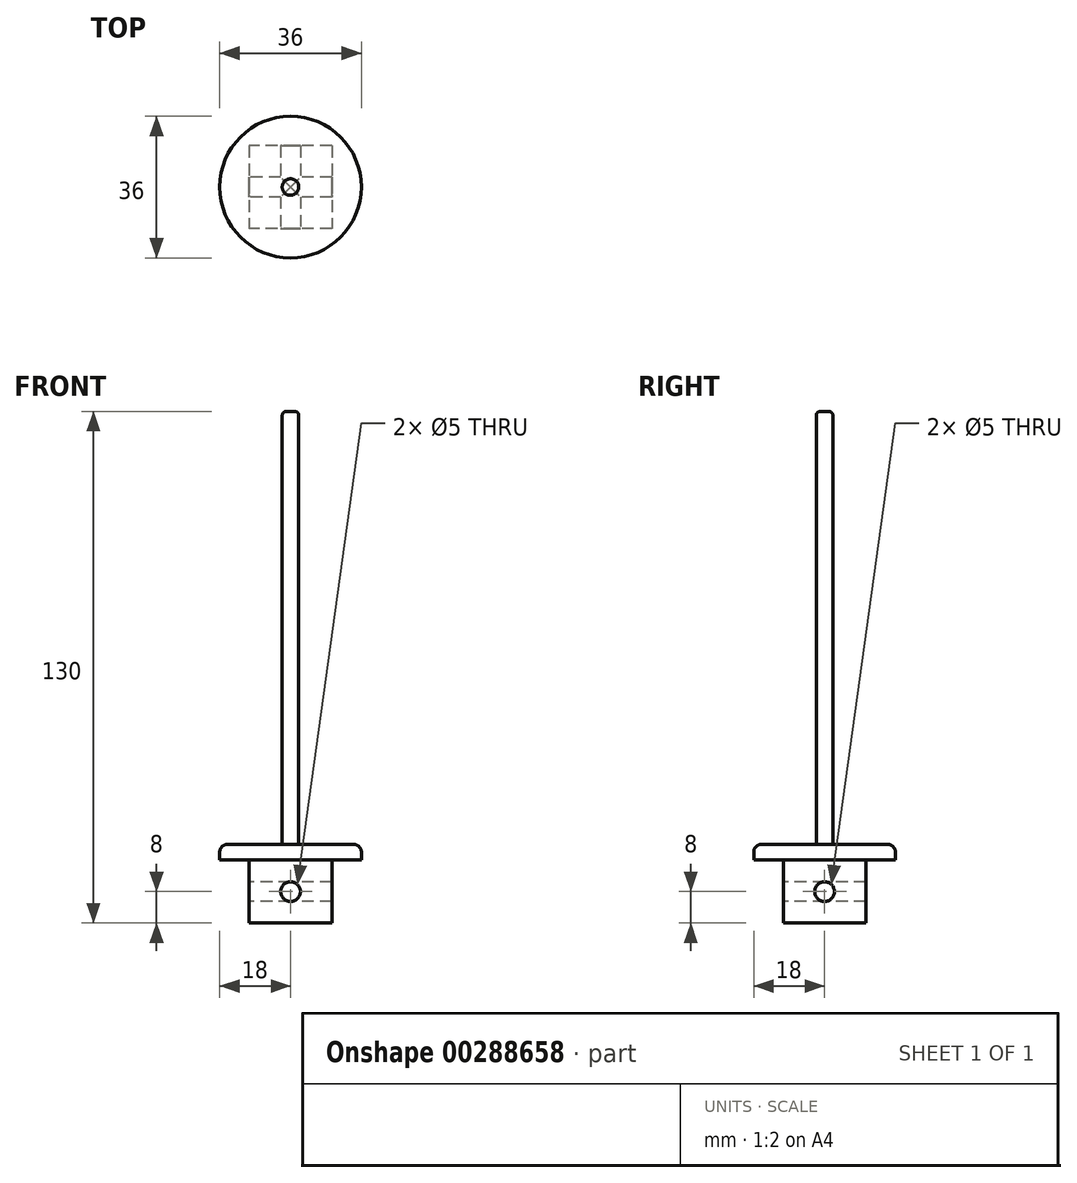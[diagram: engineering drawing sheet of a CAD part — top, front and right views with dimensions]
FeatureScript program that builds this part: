
annotation { "Feature Type Name" : "Feature", "Feature Type Description" : "" }
export const myFeature = defineFeature(function(context is Context, id is Id, definition is map)
    precondition{}
    {
        {
            var Q0;
            Q0=qCreatedBy(makeId("Top.planeOp"),FACE);
            var sketch = newSketch(context, id + "F0", { "sketchPlane" : qUnion([Q0])});
            skCircle(sketch, "E0", {"center": v(0, 0) * mm, "radius": 18 * mm});
            skSolve(sketch);
        }
        {
            var Q0;
            Q0 = qSketchRegion(id + "F0", true);
            extrude(context, id + "F1", {"entities" : qUnion([Q0]), "depth" : 4 * mm});
        }
        {
            var Q0;
            Q0=qCreatedBy(makeId("Top.planeOp"),FACE);
            var sketch = newSketch(context, id + "F2", { "sketchPlane" : qUnion([Q0])});
            skLineSegment(sketch, "E1.bottom", {"start": v(10.5, 10.5) * mm, "end": v(-10.5, 10.5) * mm});
            skLineSegment(sketch, "E1.top", {"start": v(10.5, -10.5) * mm, "end": v(-10.5, -10.5) * mm});
            skLineSegment(sketch, "E1.left", {"start": v(10.5, 10.5) * mm, "end": v(10.5, -10.5) * mm});
            skLineSegment(sketch, "E1.right", {"start": v(-10.5, 10.5) * mm, "end": v(-10.5, -10.5) * mm});
            skPoint(sketch, "E1.middle", {"position": v(0, 0) * mm});
            skSolve(sketch);
        }
        {
            var Q0;
            Q0=makeQuery(id+"F2.imprint","IMPRINT",FACE,{"disambiguationData":[TD([[makeQuery(id+"F2.imprint","IMPRINT",EDGE,{"derivedFrom":sQuery(id+"F2.wireOp",EDGE,"E1.bottom")}),1.0]])]});
            var Q1;
            Q1=sQuery(id+"F2.wireOp",EDGE,"E1.bottom");
            var Q2;
            Q2=sQuery(id+"F2.wireOp",EDGE,"E1.top");
            var Q3;
            Q3=sQuery(id+"F2.wireOp",EDGE,"E1.left");
            var Q4;
            Q4=sQuery(id+"F2.wireOp",EDGE,"E1.right");
            extrude(context, id + "F3", {"entities" : qUnion([Q0]), "operationType" : NewBodyOperationType.ADD, "surfaceEntities" : qUnion([Q1, Q2, Q3, Q4]), "oppositeDirection" : true, "depth" : 16 * mm});
        }
        {
            var Q0;
            Q0=makeQuery(id+"F1.opExtrude","CAP_FACE",FACE,{"disambiguationData":[OSD([sQuery(id+"F0.wireOp",EDGE,"E0")])],"isStart":false});
            var sketch = newSketch(context, id + "F4", { "sketchPlane" : qUnion([Q0])});
            skCircle(sketch, "E2", {"center": v(0, 0) * mm, "radius": 2.1 * mm});
            skSolve(sketch);
        }
        {
            var Q0;
            Q0=makeQuery(id+"F4.imprint","IMPRINT",FACE,{"disambiguationData":[TD([[makeQuery(id+"F4.imprint","IMPRINT",EDGE,{"derivedFrom":sQuery(id+"F4.wireOp",EDGE,"E2")}),1.0]])]});
            var Q1;
            Q1=sQuery(id+"F4.wireOp",EDGE,"E2");
            extrude(context, id + "F5", {"entities" : qUnion([Q0]), "operationType" : NewBodyOperationType.REMOVE, "surfaceEntities" : qUnion([Q1]), "endBound" : BoundingType.THROUGH_ALL, "oppositeDirection" : true, "depth" : 20 * mm});
        }
        {
            var Q0;
            Q0=makeQuery(id+"F1.opExtrude","CAP_EDGE",EDGE,{"disambiguationData":[OSD([sQuery(id+"F0.wireOp",EDGE,"E0")])],"isStart":false});
            fillet(context, id + "F6", {"entities" : qUnion([Q0]), "radius" : 2 * mm, "tangentPropagation" : true, "allowEdgeOverflow" : false});
        }
        {
            var Q0;
            Q0=makeQuery(id+"F3.opExtrude","CAP_FACE",FACE,{"disambiguationData":[OSD([sQuery(id+"F2.wireOp",EDGE,"E1.bottom"),sQuery(id+"F2.wireOp",EDGE,"E1.top"),sQuery(id+"F2.wireOp",EDGE,"E1.left"),sQuery(id+"F2.wireOp",EDGE,"E1.right")])],"isStart":false});
            var sketch = newSketch(context, id + "F7", { "sketchPlane" : qUnion([Q0])});
            skCircle(sketch, "E3", {"center": v(0, 0) * mm, "radius": 2.1 * mm});
            skSolve(sketch);
        }
        {
            var Q0;
            Q0 = qSketchRegion(id + "F7", true);
            extrude(context, id + "F8", {"entities" : qUnion([Q0]), "operationType" : NewBodyOperationType.ADD, "oppositeDirection" : true, "depth" : 130 * mm});
        }
        {
            var Q0;
            Q0=makeQuery(id+"F8.opExtrude","CAP_EDGE",EDGE,{"disambiguationData":[OSD([sQuery(id+"F7.wireOp",EDGE,"E3")])],"isStart":false});
            fillet(context, id + "F9", {"entities" : qUnion([Q0]), "radius" : 1 * mm, "tangentPropagation" : true, "allowEdgeOverflow" : false});
        }
        {
            var Q0;
            Q0=makeQuery(id+"F3.opExtrude","SWEPT_FACE",FACE,{"disambiguationData":[OSD([sQuery(id+"F2.wireOp",EDGE,"E1.top")])]});
            var sketch = newSketch(context, id + "F10", { "sketchPlane" : qUnion([Q0])});
            skCircle(sketch, "E4", {"center": v(0, -8) * mm, "radius": 2.5 * mm});
            skSolve(sketch);
        }
        {
            var Q0;
            Q0=makeQuery(id+"F10.imprint","IMPRINT",FACE,{"disambiguationData":[TD([[makeQuery(id+"F10.imprint","IMPRINT",EDGE,{"derivedFrom":sQuery(id+"F10.wireOp",EDGE,"E4")}),1.0]])]});
            extrude(context, id + "F11", {"entities" : qUnion([Q0]), "operationType" : NewBodyOperationType.REMOVE, "oppositeDirection" : true, "depth" : 25 * mm, "offsetDistance" : 25 * mm});
        }
        {
            var Q0;
            Q0=makeQuery(id+"F3.opExtrude","SWEPT_FACE",FACE,{"disambiguationData":[OSD([sQuery(id+"F2.wireOp",EDGE,"E1.right")])]});
            var sketch = newSketch(context, id + "F12", { "sketchPlane" : qUnion([Q0])});
            skCircle(sketch, "E5", {"center": v(0, -8) * mm, "radius": 2.5 * mm});
            skPoint(sketch, "E5.centerSnap0", {"position": v(0, 0) * mm});
            skSolve(sketch);
        }
        {
            var Q0;
            Q0=makeQuery(id+"F12.imprint","IMPRINT",FACE,{"disambiguationData":[TD([[makeQuery(id+"F12.imprint","IMPRINT",EDGE,{"derivedFrom":sQuery(id+"F12.wireOp",EDGE,"E5")}),1.0]])]});
            extrude(context, id + "F13", {"entities" : qUnion([Q0]), "operationType" : NewBodyOperationType.REMOVE, "oppositeDirection" : true, "depth" : 25 * mm, "offsetDistance" : 25 * mm});
        }
    });
